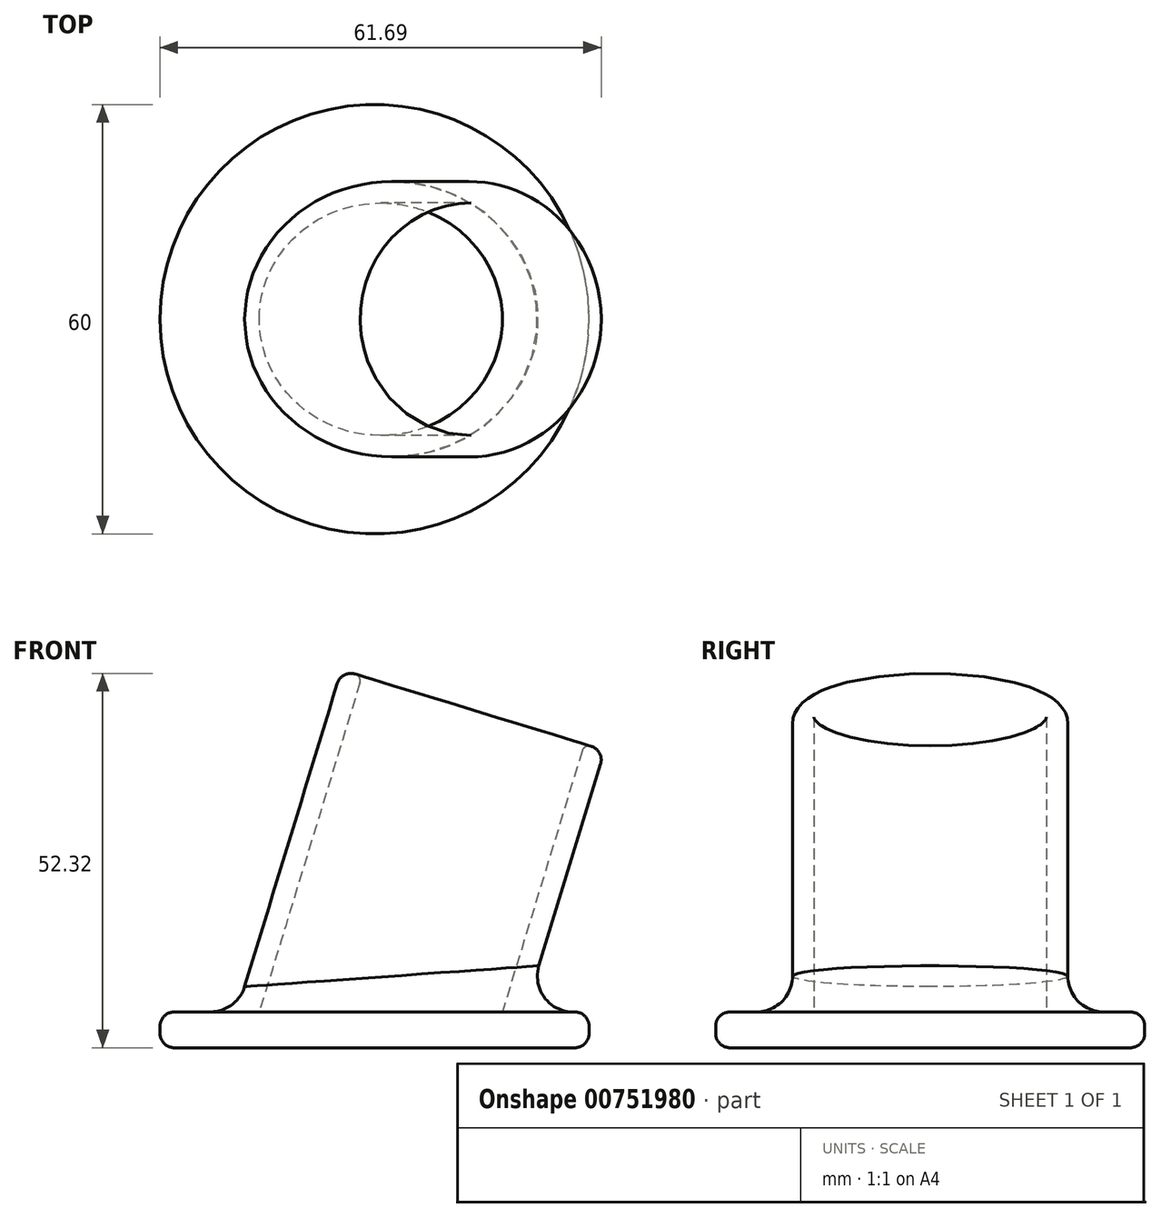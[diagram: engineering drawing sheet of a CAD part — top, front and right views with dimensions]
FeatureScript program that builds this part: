
annotation { "Feature Type Name" : "Feature", "Feature Type Description" : "" }
export const myFeature = defineFeature(function(context is Context, id is Id, definition is map)
    precondition{}
    {
        {
            var Q0;
            Q0=qCreatedBy(makeId("Front.planeOp"),FACE);
            var sketch = newSketch(context, id + "F0", { "sketchPlane" : qUnion([Q0])});
            skLineSegment(sketch, "E0.left", {"start": v(-1.76, 46.94) * mm, "end": v(-16.38, -0.88) * mm});
            skLineSegment(sketch, "E1", {"start": v(-0.84, -5.63) * mm, "end": v(13.78, 42.19) * mm});
            skLineSegment(sketch, "E2.0", {"start": v(-4.63, 47.82) * mm, "end": v(-19.25, 0) * mm});
            skLineSegment(sketch, "E3", {"start": v(-4.63, 47.82) * mm, "end": v(-1.76, 46.94) * mm});
            skLineSegment(sketch, "E4", {"start": v(-16.38, -0.88) * mm, "end": v(-19.25, 0) * mm});
            skSolve(sketch);
        }
        {
            var Q0;
            Q0=makeQuery(id+"F0.imprint","IMPRINT",FACE,{"disambiguationData":[TD([[makeQuery(id+"F0.imprint","IMPRINT",EDGE,{"derivedFrom":sQuery(id+"F0.wireOp",EDGE,"E0.left")}),-1.0]])]});
            var Q1;
            Q1=sQuery(id+"F0.wireOp",EDGE,"E1");
            revolve(context, id + "F1", {"surfaceOperationType" : NewSurfaceOperationType.NEW, "entities" : qUnion([Q0]), "axis" : qUnion([Q1]), "revolveType" : RevolveType.FULL});
        }
        {
            var Q0;
            Q0=qCreatedBy(makeId("Front.planeOp"),FACE);
            var sketch = newSketch(context, id + "F2", { "sketchPlane" : qUnion([Q0])});
            skLineSegment(sketch, "E5.bottom", {"start": v(-30, 0) * mm, "end": v(0, 0) * mm});
            skLineSegment(sketch, "E5.top", {"start": v(-30, -5) * mm, "end": v(0, -5) * mm});
            skLineSegment(sketch, "E5.left", {"start": v(-30, 0) * mm, "end": v(-30, -5) * mm});
            skLineSegment(sketch, "E6", {"start": v(0, 0) * mm, "end": v(0, -5) * mm});
            skPoint(sketch, "E7.firstSnap0", {"position": v(-15, -5) * mm});
            skLineSegment(sketch, "E7.bottom", {"start": v(-15, -2.24) * mm, "end": v(24.6, -2.24) * mm});
            skLineSegment(sketch, "E7.top", {"start": v(-15, -13.23) * mm, "end": v(24.6, -13.23) * mm});
            skLineSegment(sketch, "E7.left", {"start": v(-15, -2.24) * mm, "end": v(-15, -13.23) * mm});
            skLineSegment(sketch, "E7.right", {"start": v(24.6, -2.24) * mm, "end": v(24.6, -13.23) * mm});
            skSolve(sketch);
        }
        {
            var Q0;
            {var subQ0=sQuery(id+"F2.wireOp",EDGE,"E7.top");Q0=makeQuery(id+"F2.imprint","IMPRINT",FACE,{"disambiguationData":[TD([[makeQuery(id+"F2.imprint","IMPRINT",EDGE,{"derivedFrom":subQ0}),1.0]])]});}
            var Q1;
            {var subQ0=sQuery(id+"F2.wireOp",EDGE,"E6");var subQ1=sQuery(id+"F2.wireOp",EDGE,"E5.top");var subQ2=makeQuery(id+"F2.imprint","INTERSECT",VERTEX,{"derivedFrom":[subQ1,subQ0]});Q1=makeQuery(id+"F2.imprint","IMPRINT",FACE,{"disambiguationData":[TD([[makeQuery(id+"F2.imprint","IMPRINT",EDGE,{"disambiguationData":[TD([[subQ2,1.0]])],"derivedFrom":subQ1}),1.0]])]});}
            extrude(context, id + "F3", {"entities" : qUnion([Q0, Q1]), "operationType" : NewBodyOperationType.REMOVE, "endBound" : BoundingType.SYMMETRIC, "oppositeDirection" : true, "depth" : 60 * mm, "offsetDistance" : 25 * mm});
        }
        {
            var Q0;
            Q0=makeQuery(id+"F2.imprint","IMPRINT",FACE,{"disambiguationData":[TD([[makeQuery(id+"F2.imprint","IMPRINT",EDGE,{"derivedFrom":sQuery(id+"F2.wireOp",EDGE,"E5.bottom")}),-1.0]])]});
            var Q1;
            {var subQ0=sQuery(id+"F2.wireOp",EDGE,"E6");var subQ1=sQuery(id+"F2.wireOp",EDGE,"E5.top");var subQ2=makeQuery(id+"F2.imprint","INTERSECT",VERTEX,{"derivedFrom":[subQ1,subQ0]});Q1=makeQuery(id+"F2.imprint","IMPRINT",FACE,{"disambiguationData":[TD([[makeQuery(id+"F2.imprint","IMPRINT",EDGE,{"disambiguationData":[TD([[subQ2,1.0]])],"derivedFrom":subQ1}),1.0]])]});}
            var Q2;
            Q2=sQuery(id+"F2.wireOp",EDGE,"E6");
            revolve(context, id + "F4", {"operationType" : NewBodyOperationType.ADD, "surfaceOperationType" : NewSurfaceOperationType.NEW, "entities" : qUnion([Q0, Q1]), "axis" : qUnion([Q2]), "revolveType" : RevolveType.FULL});
        }
        {
            var Q0;
            Q0=makeQuery(id+"F4.boolean.opBoolean","INTERSECT",EDGE,{"derivedFrom":[makeQuery(id+"F1.opRevolve","SWEPT_FACE",FACE,{"disambiguationData":[OSD([sQuery(id+"F0.wireOp",EDGE,"E2.0")])]}),makeQuery(id+"F4.opRevolve","SWEPT_FACE",FACE,{"disambiguationData":[OSD([sQuery(id+"F2.wireOp",EDGE,"E5.bottom")])]})]});
            fillet(context, id + "F5", {"entities" : qUnion([Q0]), "radius" : 5 * mm, "tangentPropagation" : true, "allowEdgeOverflow" : false});
        }
        {
            var Q0;
            Q0=makeQuery(id+"F1.opRevolve","SWEPT_EDGE",EDGE,{"disambiguationData":[OSD([sQuery(id+"F0.wireOp",EDGE,"E2.0"),sQuery(id+"F0.wireOp",EDGE,"E3")])]});
            var Q1;
            Q1=makeQuery(id+"F4.opRevolve","SWEPT_EDGE",EDGE,{"disambiguationData":[OSD([sQuery(id+"F2.wireOp",EDGE,"E5.bottom"),sQuery(id+"F2.wireOp",EDGE,"E5.left")])]});
            var Q2;
            Q2=makeQuery(id+"F4.opRevolve","SWEPT_EDGE",EDGE,{"disambiguationData":[OSD([sQuery(id+"F2.wireOp",EDGE,"E5.top"),sQuery(id+"F2.wireOp",EDGE,"E5.left")])]});
            fillet(context, id + "F6", {"entities" : qUnion([Q0, Q1, Q2]), "radius" : 2 * mm, "tangentPropagation" : true, "allowEdgeOverflow" : false});
        }
        {
            var Q0;
            Q0=makeQuery(id+"F1.opRevolve","SWEPT_EDGE",EDGE,{"disambiguationData":[OSD([sQuery(id+"F0.wireOp",EDGE,"E0.left"),sQuery(id+"F0.wireOp",EDGE,"E3")])]});
            fillet(context, id + "F7", {"entities" : qUnion([Q0]), "radius" : 1 * mm, "tangentPropagation" : true, "allowEdgeOverflow" : false});
        }
    });
